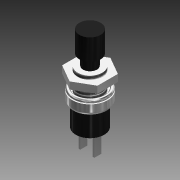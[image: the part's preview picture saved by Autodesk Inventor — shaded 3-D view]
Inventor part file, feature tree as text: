
AUTODESK INVENTOR PART (.ipt)
format: ipt  version: 2013 SP1 (Build 170176100, 176)  size: 225,280 bytes
history: native  units: mm
features: sketch x8, extrude x7, other x6, fillet x1, thread x1, revolve x1
ambient origin geometry x8: Origin, YZ Plane, XZ Plane, XY Plane, X Axis, Y Axis, Z Axis, Center Point
bodies: Volumenkörper1 (feature_tree), Volumenkörper2 (feature_tree), Volumenkörper3 (feature_tree), Volumenkörper4 (feature_tree), Volumenkörper5 (feature_tree), Volumenkörper6 (feature_tree), Volumenkörper7 (feature_tree)
feature tree (24):
  extrude  "Extrusion1"  Depth=3.0mm TaperAngle=0.0deg
  fillet  "Rundung1"  Radius=1.0mm
  extrude  "Extrusion2"  Depth=6.0mm TaperAngle=0.0deg
  thread  "Gewinde1"  [1 undecoded]
  extrude  "Extrusion3"  Depth=3.0mm TaperAngle=0.0deg
  other  "Körper verschieben1"
  extrude  "Extrusion4"  Depth=6.0mm
  other  "Körper verschieben2"
  extrude  "Extrusion5"  Depth=9.0mm TaperAngle=0.0deg
  other  "Körper verschieben3"
  extrude  "Extrusion6"  Depth=6.0mm TaperAngle=0.0deg
  other  "Körper verschieben4"
  revolve  "Umdrehung1"
  other  "Körper verschieben5"
  extrude  "Extrusion7"  Depth=0.5mm
  other  "Körper verschieben6"
  sketch  "Skizze1"  dims[d0=10.0mm d1=3.0mm d2=0.0mm d3=1.0mm]
  sketch  "Skizze2"  dims[d4=7.0mm d5=6.0mm d6=0.0mm d7=10.0mm d8=0.0mm]
  sketch  "Skizze3"  dims[d9=4.0mm d10=3.0mm d11=0.0mm]
  sketch  "Skizze4"  dims[d12=0.0mm d13=0.0mm d14=6.0mm d15=6.0mm]
  sketch  "Skizze5"  dims[d16=6.0mm d17=0.0mm d18=0.0mm d19=0.0mm d20=9.0mm]
  sketch  "Skizze6"  dims[d21=8.0mm d22=6.0mm d23=0.0mm]
  sketch  "Skizze8"  dims[d24=0.0mm d25=0.0mm d26=-3.0mm d27=0.5mm]
  sketch  "Skizze9"  dims[d28=2.0mm d29=0.5mm d30=2.0mm d31=6.0mm d32=0.0mm d33=0.0mm d34=0.0mm d35=-9.0mm d36=1.0mm d37=4.5mm d38=90.0deg d39=0.0mm d40=0.0mm d41=0.5mm d44=7.0mm d45=2.0mm d46=0.0mm d47=0.0mm d48=0.0mm d49=3.0mm]
note: 1 required parameter value undecoded (feature->parameter linkage not recoverable at this tier; creation-order binding heuristic only, values carry confidence <= 0.55)
